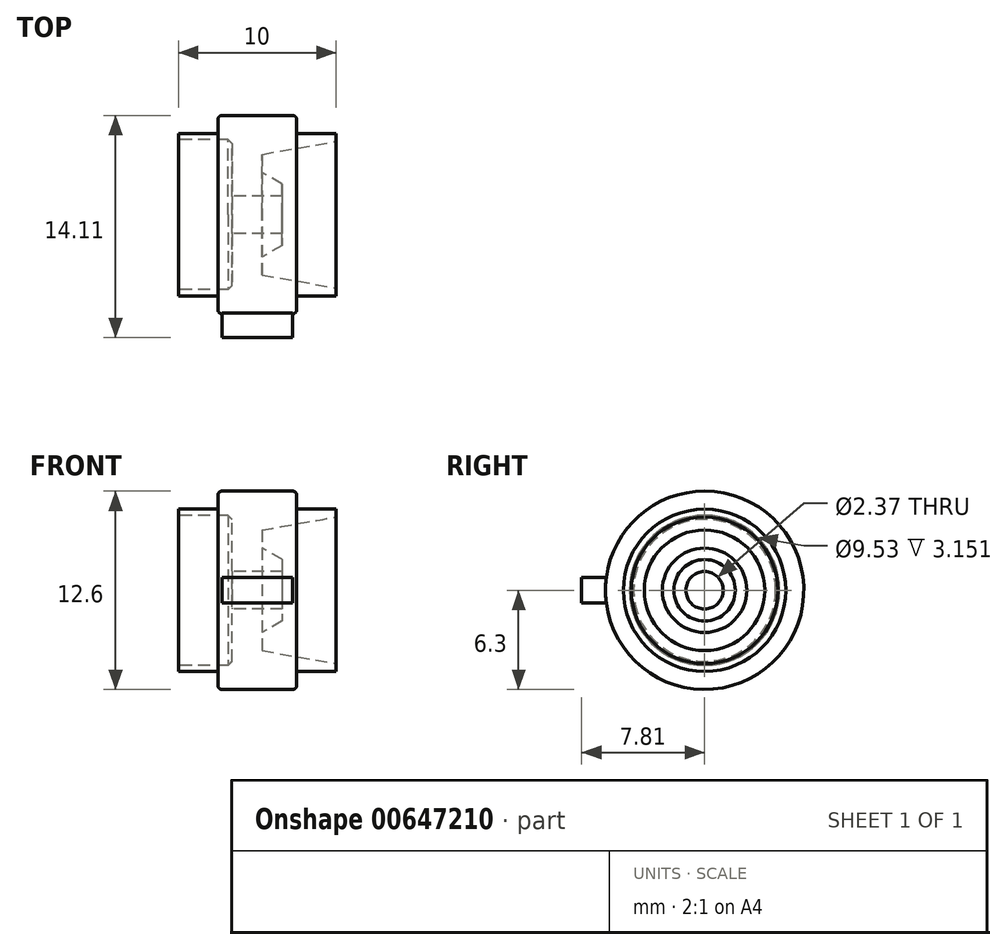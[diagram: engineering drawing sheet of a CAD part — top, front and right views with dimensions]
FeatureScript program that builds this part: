
annotation { "Feature Type Name" : "Feature", "Feature Type Description" : "" }
export const myFeature = defineFeature(function(context is Context, id is Id, definition is map)
    precondition{}
    {
        {
            var Q0;
            Q0=qCreatedBy(makeId("Front.planeOp"),FACE);
            var sketch = newSketch(context, id + "F0", { "sketchPlane" : qUnion([Q0])});
            skLineSegment(sketch, "E0", {"start": v(0, -1.19) * mm, "end": v(0, -6.3) * mm, "construction": true});
            skLineSegment(sketch, "E1", {"start": v(0, -6.3) * mm, "end": v(-2.25, -6.3) * mm});
            skLineSegment(sketch, "E2", {"start": v(-2.5, -6.05) * mm, "end": v(-2.5, -5.16) * mm});
            skLineSegment(sketch, "E3", {"start": v(-2.5, -5.16) * mm, "end": v(-5, -5.16) * mm});
            skLineSegment(sketch, "E4", {"start": v(-5, -5.16) * mm, "end": v(-5, -4.76) * mm});
            skLineSegment(sketch, "E5", {"start": v(-5, -4.76) * mm, "end": v(-1.6, -4.76) * mm});
            skLineSegment(sketch, "E6", {"start": v(0, -1.19) * mm, "end": v(0, -1.19) * mm});
            skLineSegment(sketch, "E7", {"start": v(0, -1.19) * mm, "end": v(0, 0) * mm, "construction": true});
            skCircle(sketch, "E8", {"center": v(0, -9.3) * mm, "radius": 2.77 * mm, "construction": true});
            skLineSegment(sketch, "E9", {"start": v(1.95, 0) * mm, "end": v(11.37, 0) * mm, "construction": true});
            skLineSegment(sketch, "E10", {"start": v(-1.6, -4.76) * mm, "end": v(-1.6, -1.19) * mm});
            skLineSegment(sketch, "E11", {"start": v(-1.6, -1.19) * mm, "end": v(0, -1.19) * mm});
            skLineSegment(sketch, "E12", {"start": v(0, -6.3) * mm, "end": v(2.25, -6.3) * mm});
            skLineSegment(sketch, "E13", {"start": v(2.5, -6.05) * mm, "end": v(2.5, -5.16) * mm});
            skLineSegment(sketch, "E14", {"start": v(2.5, -5.16) * mm, "end": v(5, -5.16) * mm});
            skLineSegment(sketch, "E15", {"start": v(5, -5.16) * mm, "end": v(5, -4.66) * mm});
            skLineSegment(sketch, "E16", {"start": v(0.3, -3.83) * mm, "end": v(5, -4.66) * mm});
            skLineSegment(sketch, "E17", {"start": v(1.58, -1.19) * mm, "end": v(0, -1.19) * mm});
            skPoint(sketch, "E18.visualSharp", {"position": v(-2.5, -6.3) * mm});
            skArc(sketch, "E18.filletArc", {"start": v(-2.5, -6.05) * mm, "mid": v(-2.43, -6.22) * mm, "end": v(-2.25, -6.3) * mm});
            skPoint(sketch, "E19.visualSharp", {"position": v(2.5, -6.3) * mm});
            skArc(sketch, "E19.filletArc", {"start": v(2.25, -6.3) * mm, "mid": v(2.43, -6.22) * mm, "end": v(2.5, -6.05) * mm});
            skLineSegment(sketch, "E20", {"start": v(1.58, -1.19) * mm, "end": v(1.58, -1.95) * mm});
            skLineSegment(sketch, "E21", {"start": v(1.58, -1.95) * mm, "end": v(0.3, -2.68) * mm});
            skLineSegment(sketch, "E22", {"start": v(0.3, -2.68) * mm, "end": v(0.3, -3.83) * mm});
            skSolve(sketch);
        }
        {
            var Q0;
            Q0 = qSketchRegion(id + "F0", true);
            var Q1;
            Q1=sQuery(id+"F0.wireOp",EDGE,"E9");
            revolve(context, id + "F1", {"entities" : qUnion([Q0]), "axis" : qUnion([Q1]), "revolveType" : RevolveType.FULL});
        }
        {
            var Q0;
            Q0=makeQuery(id+"F1.opRevolve","SWEPT_EDGE",EDGE,{"disambiguationData":[OSD([sQuery(id+"F0.wireOp",EDGE,"E5"),sQuery(id+"F0.wireOp",EDGE,"E10")])]});
            chamfer(context, id + "F2", {"entities" : qUnion([Q0]), "width" : 0.25 * mm, "tangentPropagation" : true});
        }
        {
            var Q0;
            Q0=qCreatedBy(makeId("Front.planeOp"),FACE);
            cPlane(context, id + "F3", {"entities" : qUnion([Q0]), "cplaneType" : CPlaneType.OFFSET, "offset" : 4.76 * mm, "width" : 152.4 * mm, "height" : 152.4 * mm});
        }
        {
            var Q0;
            Q0=qCreatedBy(id+"F3.planeOp",FACE);
            var sketch = newSketch(context, id + "F4", { "sketchPlane" : qUnion([Q0])});
            skLineSegment(sketch, "E23.bottom", {"start": v(-2.25, 0.8) * mm, "end": v(2.25, 0.8) * mm});
            skLineSegment(sketch, "E23.top", {"start": v(-2.25, -0.8) * mm, "end": v(2.25, -0.8) * mm});
            skLineSegment(sketch, "E23.left", {"start": v(-2.25, 0.8) * mm, "end": v(-2.25, -0.8) * mm});
            skLineSegment(sketch, "E23.right", {"start": v(2.25, 0.8) * mm, "end": v(2.25, -0.8) * mm});
            skLineSegment(sketch, "E24", {"start": v(-2.25, 0.8) * mm, "end": v(2.25, -0.8) * mm, "construction": true});
            skSolve(sketch);
        }
        {
            var Q0;
            Q0 = qSketchRegion(id + "F4", true);
            extrude(context, id + "F5", {"entities" : qUnion([Q0]), "operationType" : NewBodyOperationType.ADD, "depth" : 3.05 * mm, "offsetDistance" : 25.4 * mm});
        }
    });
